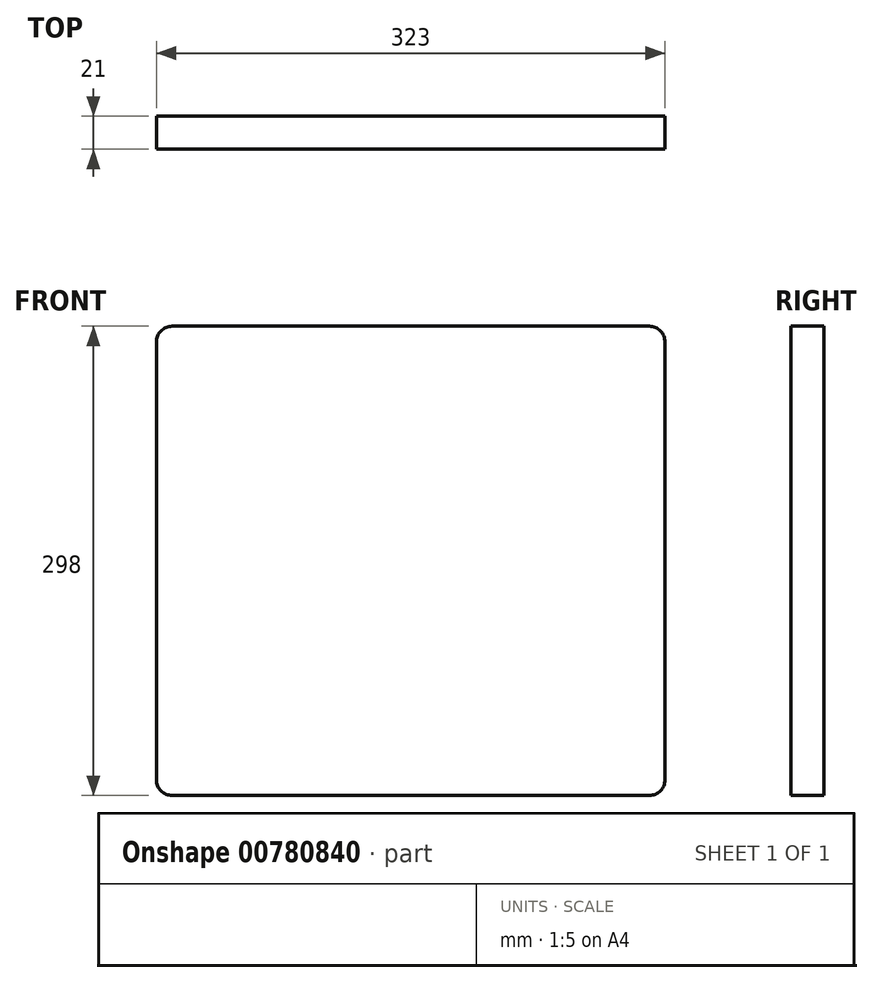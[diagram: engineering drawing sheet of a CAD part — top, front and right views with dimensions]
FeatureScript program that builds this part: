
annotation { "Feature Type Name" : "Feature", "Feature Type Description" : "" }
export const myFeature = defineFeature(function(context is Context, id is Id, definition is map)
    precondition{}
    {
        {
            var Q0;
            Q0=qCreatedBy(makeId("Front.planeOp"),FACE);
            var sketch = newSketch(context, id + "F0", { "sketchPlane" : qUnion([Q0])});
            skLineSegment(sketch, "E0.bottom", {"start": v(-151.5, 149) * mm, "end": v(151.5, 149) * mm});
            skLineSegment(sketch, "E0.top", {"start": v(-151.5, -149) * mm, "end": v(151.5, -149) * mm});
            skLineSegment(sketch, "E0.left", {"start": v(-161.5, 139) * mm, "end": v(-161.5, -139) * mm});
            skLineSegment(sketch, "E0.right", {"start": v(161.5, 139) * mm, "end": v(161.5, -139) * mm});
            skPoint(sketch, "E0.middle", {"position": v(0, 0) * mm});
            skLineSegment(sketch, "E1.bottom", {"start": v(-19, -87.5) * mm, "end": v(19, -87.5) * mm});
            skLineSegment(sketch, "E1.top", {"start": v(-19, -138.5) * mm, "end": v(19, -138.5) * mm});
            skLineSegment(sketch, "E1.left", {"start": v(-19, -87.5) * mm, "end": v(-19, -138.5) * mm});
            skLineSegment(sketch, "E1.right", {"start": v(19, -87.5) * mm, "end": v(19, -138.5) * mm});
            skPoint(sketch, "E2.visualSharp", {"position": v(-161.5, 149) * mm});
            skArc(sketch, "E2.filletArc", {"start": v(-151.5, 149) * mm, "mid": v(-158.57, 146.07) * mm, "end": v(-161.5, 139) * mm});
            skPoint(sketch, "E3.visualSharp", {"position": v(161.5, 149) * mm});
            skArc(sketch, "E3.filletArc", {"start": v(161.5, 139) * mm, "mid": v(158.57, 146.07) * mm, "end": v(151.5, 149) * mm});
            skPoint(sketch, "E4.visualSharp", {"position": v(161.5, -149) * mm});
            skArc(sketch, "E4.filletArc", {"start": v(151.5, -149) * mm, "mid": v(158.57, -146.07) * mm, "end": v(161.5, -139) * mm});
            skPoint(sketch, "E5.visualSharp", {"position": v(-161.5, -149) * mm});
            skArc(sketch, "E5.filletArc", {"start": v(-161.5, -139) * mm, "mid": v(-158.57, -146.07) * mm, "end": v(-151.5, -149) * mm});
            skSolve(sketch);
        }
        {
            var Q0;
            Q0=makeQuery(id+"F0.imprint","IMPRINT",FACE,{"disambiguationData":[TD([[makeQuery(id+"F0.imprint","IMPRINT",EDGE,{"derivedFrom":sQuery(id+"F0.wireOp",EDGE,"E1.bottom")}),-1.0]])]});
            var Q1;
            Q1=makeQuery(id+"F0.imprint","IMPRINT",FACE,{"disambiguationData":[TD([[makeQuery(id+"F0.imprint","IMPRINT",EDGE,{"derivedFrom":sQuery(id+"F0.wireOp",EDGE,"E0.bottom")}),-1.0]])]});
            extrude(context, id + "F1", {"entities" : qUnion([Q0, Q1]), "depth" : 21 * mm, "offsetDistance" : 25 * mm});
        }
    });
